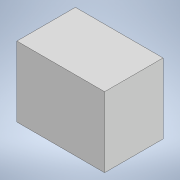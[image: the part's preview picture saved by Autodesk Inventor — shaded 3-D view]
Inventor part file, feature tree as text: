
AUTODESK INVENTOR PART (.ipt)
format: ipt  version: 2021 (Build 250183000, 183)  size: 103,424 bytes
history: native  units: in
note: dims shown in document units (in); Inventor stores cm internally (conversion verified against a paired STEP export)
features: extrude x2, sketch x2
ambient origin geometry x8: Origin, YZ Plane, XZ Plane, XY Plane, X Axis, Y Axis, Z Axis, Center Point
bodies: Body1 (feature_tree)
feature tree (4):
  extrude  "Extrusion3"  Depth=0.4724in
  extrude  "Extrusion4"  Depth=0.3937in TaperAngle=0.0deg
  sketch  "Sketch3"  dims[d17=0.1181in d19=0.4724in]
  sketch  "Sketch4"  dims[d20=0.3937in d23=0.3937in d24=0.0in d25=0.0787in d26=0.0in]
